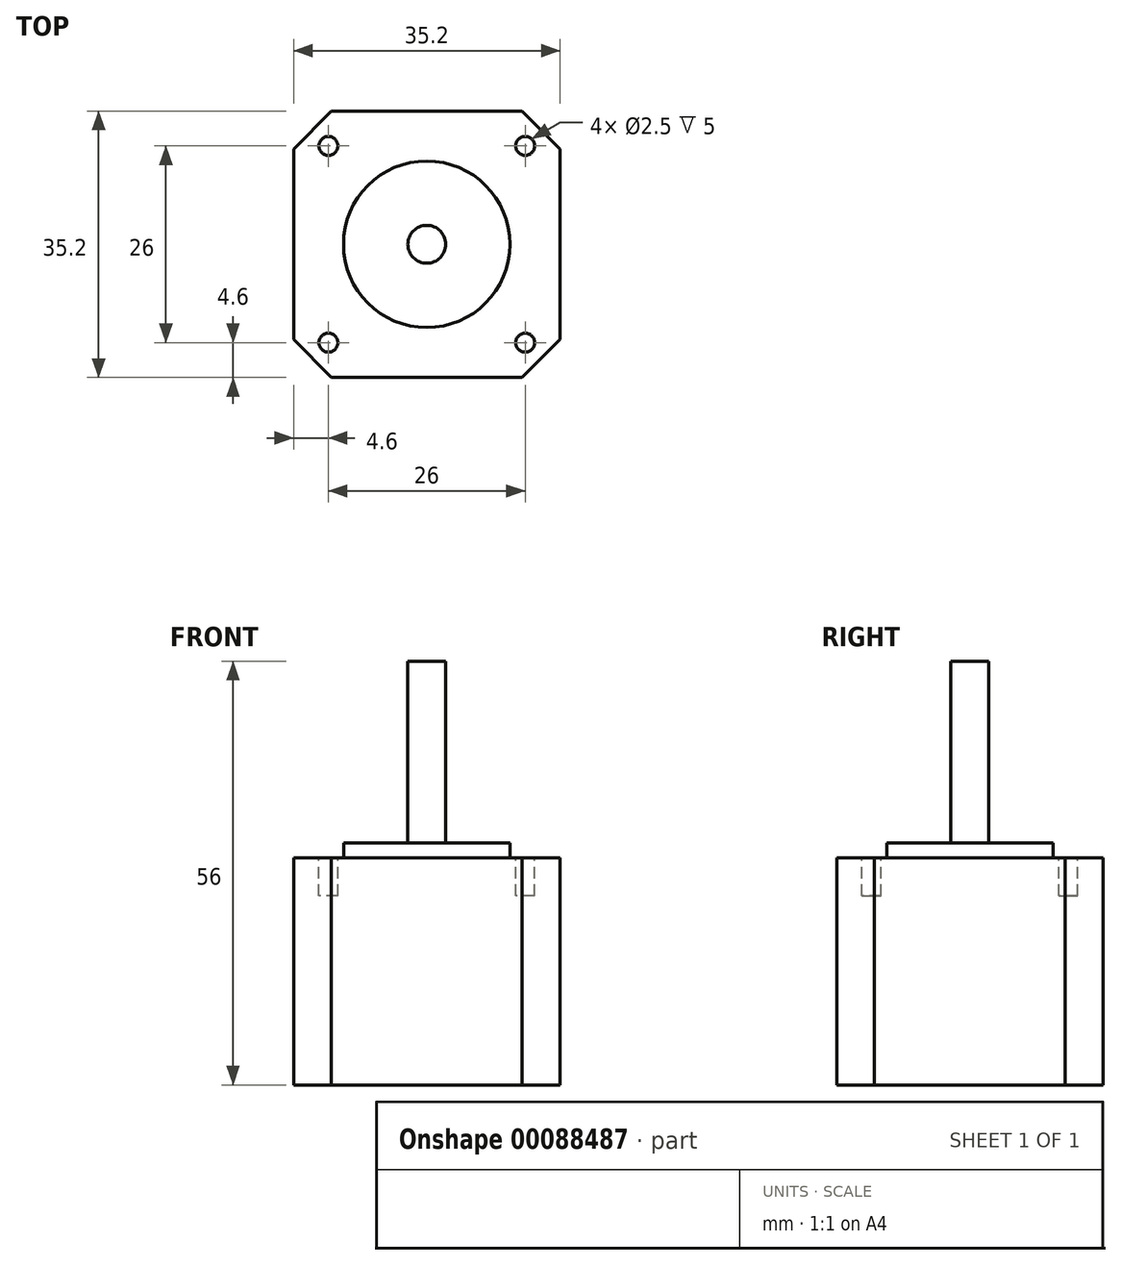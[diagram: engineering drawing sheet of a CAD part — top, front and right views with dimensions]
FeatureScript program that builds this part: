
annotation { "Feature Type Name" : "Feature", "Feature Type Description" : "" }
export const myFeature = defineFeature(function(context is Context, id is Id, definition is map)
    precondition{}
    {
        {
            var Q0;
            Q0=qCreatedBy(makeId("Top.planeOp"),FACE);
            var sketch = newSketch(context, id + "F0", { "sketchPlane" : qUnion([Q0])});
            skLineSegment(sketch, "E0.bottom", {"start": v(-17.6, 17.6) * mm, "end": v(17.6, 17.6) * mm});
            skLineSegment(sketch, "E0.top", {"start": v(-17.6, -17.6) * mm, "end": v(17.6, -17.6) * mm});
            skLineSegment(sketch, "E0.left", {"start": v(-17.6, 17.6) * mm, "end": v(-17.6, -17.6) * mm});
            skLineSegment(sketch, "E0.right", {"start": v(17.6, 17.6) * mm, "end": v(17.6, -17.6) * mm});
            skLineSegment(sketch, "E1", {"start": v(-17.6, -17.6) * mm, "end": v(17.6, 17.6) * mm, "construction": true});
            skCircle(sketch, "E2", {"center": v(0, 0) * mm, "radius": 10 * mm, "construction": true});
            skSolve(sketch);
        }
        {
            var Q0;
            Q0 = qSketchRegion(id + "F0", true);
            extrude(context, id + "F1", {"entities" : qUnion([Q0]), "depth" : 30 * mm});
        }
        {
            var Q0;
            Q0=makeQuery(id+"F1.opExtrude","SWEPT_EDGE",EDGE,{"disambiguationData":[OSD([sQuery(id+"F0.wireOp",EDGE,"E0.top"),sQuery(id+"F0.wireOp",EDGE,"E0.right")])]});
            var Q1;
            Q1=makeQuery(id+"F1.opExtrude","SWEPT_EDGE",EDGE,{"disambiguationData":[OSD([sQuery(id+"F0.wireOp",EDGE,"E0.top"),sQuery(id+"F0.wireOp",EDGE,"E0.left")])]});
            var Q2;
            Q2=makeQuery(id+"F1.opExtrude","SWEPT_EDGE",EDGE,{"disambiguationData":[OSD([sQuery(id+"F0.wireOp",EDGE,"E0.bottom"),sQuery(id+"F0.wireOp",EDGE,"E0.left")])]});
            var Q3;
            Q3=makeQuery(id+"F1.opExtrude","SWEPT_EDGE",EDGE,{"disambiguationData":[OSD([sQuery(id+"F0.wireOp",EDGE,"E0.bottom"),sQuery(id+"F0.wireOp",EDGE,"E0.right")])]});
            chamfer(context, id + "F2", {"entities" : qUnion([Q0, Q1, Q2, Q3]), "width" : 5 * mm, "tangentPropagation" : true});
        }
        {
            var Q0;
            Q0=qCreatedBy(makeId("Right.planeOp"),FACE);
            var sketch = newSketch(context, id + "F3", { "sketchPlane" : qUnion([Q0])});
            skLineSegment(sketch, "E3", {"start": v(0, 30) * mm, "end": v(0, 56) * mm});
            skLineSegment(sketch, "E4", {"start": v(0, 56) * mm, "end": v(-2.5, 56) * mm});
            skLineSegment(sketch, "E5", {"start": v(-2.5, 56) * mm, "end": v(-2.5, 32) * mm});
            skLineSegment(sketch, "E6", {"start": v(-2.5, 32) * mm, "end": v(-11, 32) * mm});
            skLineSegment(sketch, "E7", {"start": v(-11, 32) * mm, "end": v(-11, 30) * mm});
            skLineSegment(sketch, "E8", {"start": v(-11, 30) * mm, "end": v(0, 30) * mm});
            skSolve(sketch);
        }
        {
            var Q0;
            Q0=makeQuery(id+"F3.imprint","IMPRINT",FACE,{"disambiguationData":[TD([[makeQuery(id+"F3.imprint","IMPRINT",EDGE,{"derivedFrom":sQuery(id+"F3.wireOp",EDGE,"E3")}),1.0]])]});
            var Q1;
            Q1=sQuery(id+"F3.wireOp",EDGE,"E3");
            revolve(context, id + "F4", {"operationType" : NewBodyOperationType.ADD, "entities" : qUnion([Q0]), "axis" : qUnion([Q1]), "revolveType" : RevolveType.FULL});
        }
        {
            var Q0;
            Q0=makeQuery(id+"F1.opExtrude","CAP_FACE",FACE,{"disambiguationData":[OSD([sQuery(id+"F0.wireOp",EDGE,"E0.bottom"),sQuery(id+"F0.wireOp",EDGE,"E0.top"),sQuery(id+"F0.wireOp",EDGE,"E0.left"),sQuery(id+"F0.wireOp",EDGE,"E0.right")])],"isStart":false});
            var sketch = newSketch(context, id + "F5", { "sketchPlane" : qUnion([Q0])});
            skLineSegment(sketch, "E9.bottom", {"start": v(13, 13) * mm, "end": v(-13, 13) * mm, "construction": true});
            skLineSegment(sketch, "E9.top", {"start": v(13, -13) * mm, "end": v(-13, -13) * mm, "construction": true});
            skLineSegment(sketch, "E9.left", {"start": v(13, 13) * mm, "end": v(13, -13) * mm, "construction": true});
            skLineSegment(sketch, "E9.right", {"start": v(-13, 13) * mm, "end": v(-13, -13) * mm, "construction": true});
            skPoint(sketch, "E9.middle", {"position": v(0, 0) * mm});
            skCircle(sketch, "E10", {"center": v(-13, 13) * mm, "radius": 1.25 * mm});
            skCircle(sketch, "E11", {"center": v(13, 13) * mm, "radius": 1.25 * mm});
            skCircle(sketch, "E12", {"center": v(13, -13) * mm, "radius": 1.25 * mm});
            skCircle(sketch, "E13", {"center": v(-13, -13) * mm, "radius": 1.25 * mm});
            skSolve(sketch);
        }
        {
            var Q0;
            Q0 = qSketchRegion(id + "F5", true);
            extrude(context, id + "F6", {"entities" : qUnion([Q0]), "operationType" : NewBodyOperationType.REMOVE, "oppositeDirection" : true, "depth" : 5 * mm});
        }
    });
